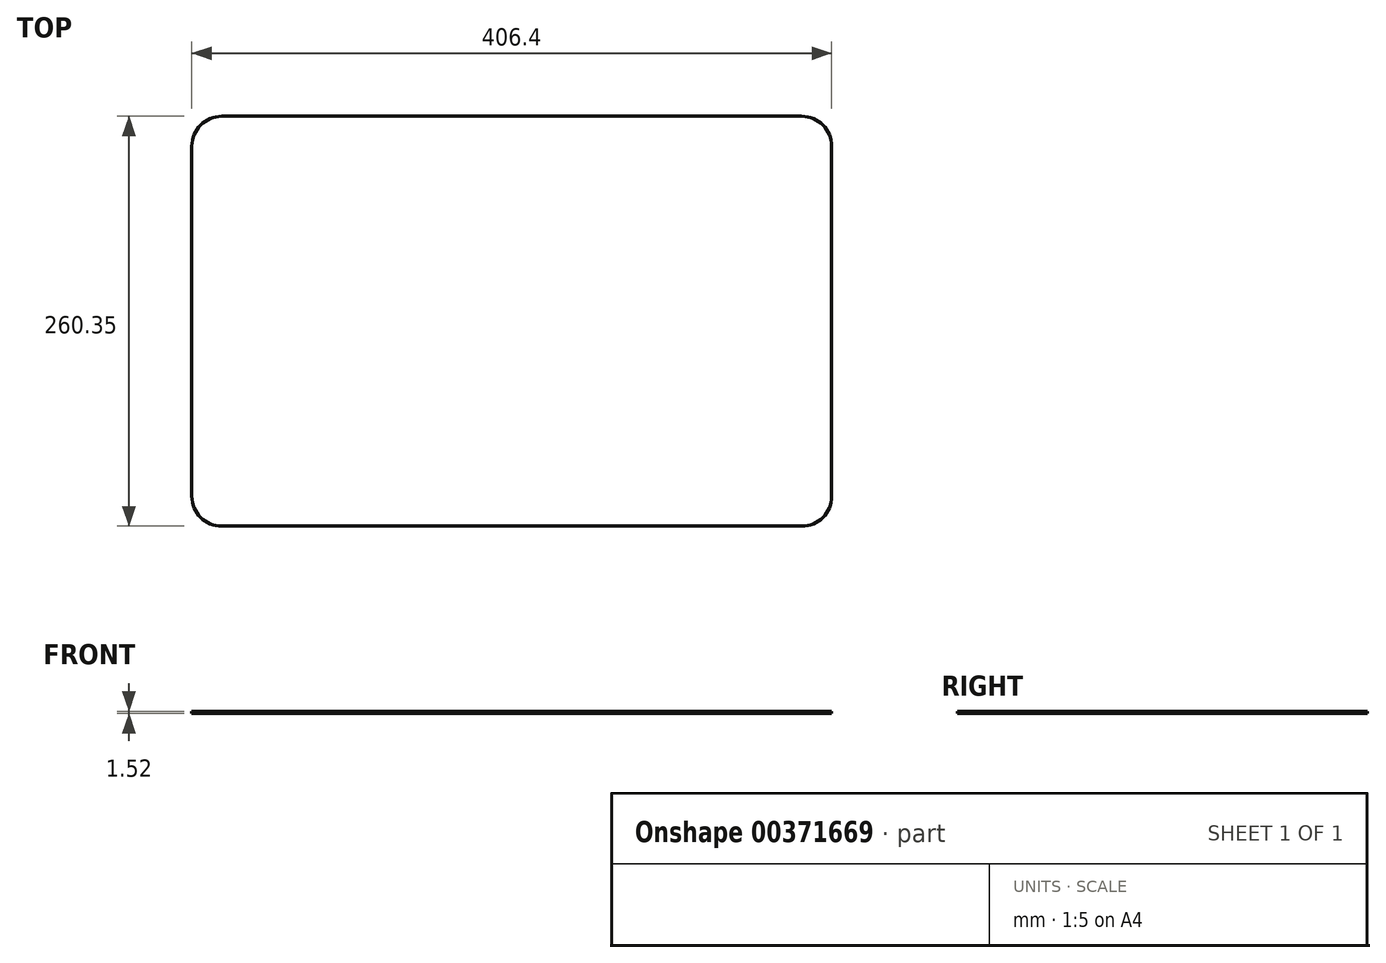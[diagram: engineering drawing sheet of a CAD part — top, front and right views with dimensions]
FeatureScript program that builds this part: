
annotation { "Feature Type Name" : "Feature", "Feature Type Description" : "" }
export const myFeature = defineFeature(function(context is Context, id is Id, definition is map)
    precondition{}
    {
        {
            var Q0;
            Q0=qCreatedBy(makeId("Top.planeOp"),FACE);
            var sketch = newSketch(context, id + "F0", { "sketchPlane" : qUnion([Q0])});
            skLineSegment(sketch, "E0.bottom", {"start": v(19.05, 0) * mm, "end": v(387.35, 0) * mm});
            skLineSegment(sketch, "E0.top", {"start": v(19.05, 260.35) * mm, "end": v(387.35, 260.35) * mm});
            skLineSegment(sketch, "E0.left", {"start": v(0, 19.05) * mm, "end": v(0, 241.3) * mm});
            skLineSegment(sketch, "E0.right", {"start": v(406.4, 19.05) * mm, "end": v(406.4, 241.3) * mm});
            skPoint(sketch, "E1.visualSharp", {"position": v(0, 260.35) * mm});
            skArc(sketch, "E1.filletArc", {"start": v(19.05, 260.35) * mm, "mid": v(5.58, 254.77) * mm, "end": v(0, 241.3) * mm});
            skPoint(sketch, "E2.visualSharp", {"position": v(0, 0) * mm});
            skArc(sketch, "E2.filletArc", {"start": v(0, 19.05) * mm, "mid": v(5.58, 5.58) * mm, "end": v(19.05, 0) * mm});
            skPoint(sketch, "E3.visualSharp", {"position": v(406.4, 0) * mm});
            skArc(sketch, "E3.filletArc", {"start": v(387.35, 0) * mm, "mid": v(400.82, 5.58) * mm, "end": v(406.4, 19.05) * mm});
            skPoint(sketch, "E4.visualSharp", {"position": v(406.4, 260.35) * mm});
            skArc(sketch, "E4.filletArc", {"start": v(406.4, 241.3) * mm, "mid": v(400.82, 254.77) * mm, "end": v(387.35, 260.35) * mm});
            skSolve(sketch);
        }
        {
            var Q0;
            Q0=makeQuery(id+"F0.imprint","IMPRINT",FACE,{"disambiguationData":[TD([[makeQuery(id+"F0.imprint","IMPRINT",EDGE,{"derivedFrom":sQuery(id+"F0.wireOp",EDGE,"E0.bottom")}),1.0]])]});
            extrude(context, id + "F1", {"entities" : qUnion([Q0]), "depth" : 1.52 * mm});
        }
    });
